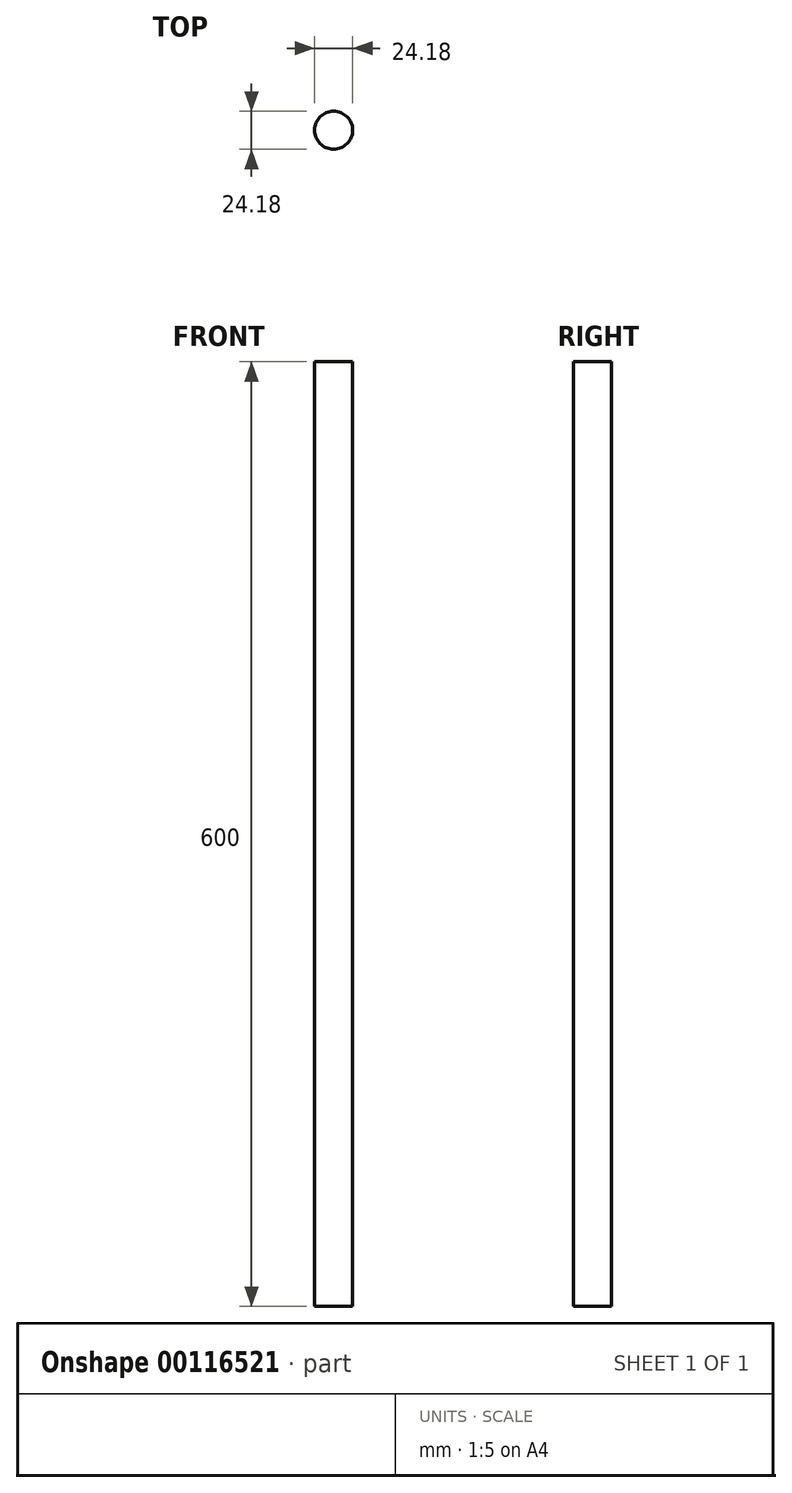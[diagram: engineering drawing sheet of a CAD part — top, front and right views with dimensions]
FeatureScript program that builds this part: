
annotation { "Feature Type Name" : "Feature", "Feature Type Description" : "" }
export const myFeature = defineFeature(function(context is Context, id is Id, definition is map)
    precondition{}
    {
        {
            var Q0;
            Q0=qCreatedBy(makeId("Top.planeOp"),FACE);
            var sketch = newSketch(context, id + "F0", { "sketchPlane" : qUnion([Q0])});
            skCircle(sketch, "E0", {"center": v(0, 0) * mm, "radius": 12.1 * mm});
            skSolve(sketch);
        }
        {
            var Q0;
            Q0 = qSketchRegion(id + "F0", true);
            var Q1;
            Q1=makeQuery(id+"F0.imprint","IMPRINT",FACE,{"disambiguationData":[TD([[makeQuery(id+"F0.imprint","IMPRINT",EDGE,{"derivedFrom":sQuery(id+"F0.wireOp",EDGE,"E0")}),1.0]])]});
            extrude(context, id + "F1", {"entities" : qUnion([Q0, Q1]), "depth" : 600 * mm});
        }
    });
